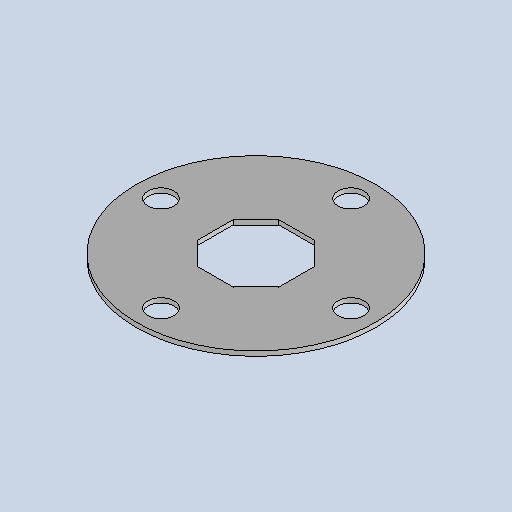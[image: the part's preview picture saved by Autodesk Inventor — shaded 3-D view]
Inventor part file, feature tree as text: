
AUTODESK INVENTOR PART (.ipt)
format: ipt  version: 2025.1 (Build 291241020, 241B)  size: 224,768 bytes
history: native  units: mm
features: other x4, sketch x2, sheet_metal_op x1, pattern_circular x1
ambient origin geometry x8: Origin, YZ Plane, XZ Plane, XY Plane, X Axis, Y Axis, Z Axis, Center Point
bodies: Body1 (feature_tree)
feature tree (8):
  sheet_metal_op  "Face3"
  pattern_circular  "Circular Pattern1"  Count=50  [1 undecoded]
  other  "Corner Chamfer2"
  sketch  "Sketch1"  dims[d156=3.0mm]
  other  "Plate5"
  sketch  "Sketch7"  dims[d157=156.0mm d158=53.0mm d159=53.0mm d160=17.0mm d161=62.0mm d162=3.0mm d163=0.0mm d164=40.0mm d165=360.0deg d167=15.0mm d168=6.0mm d169=45.0deg]
  other  "Cut1"
  other  "Definition1"
note: 1 required parameter value undecoded (feature->parameter linkage not recoverable at this tier; creation-order binding heuristic only, values carry confidence <= 0.55)
